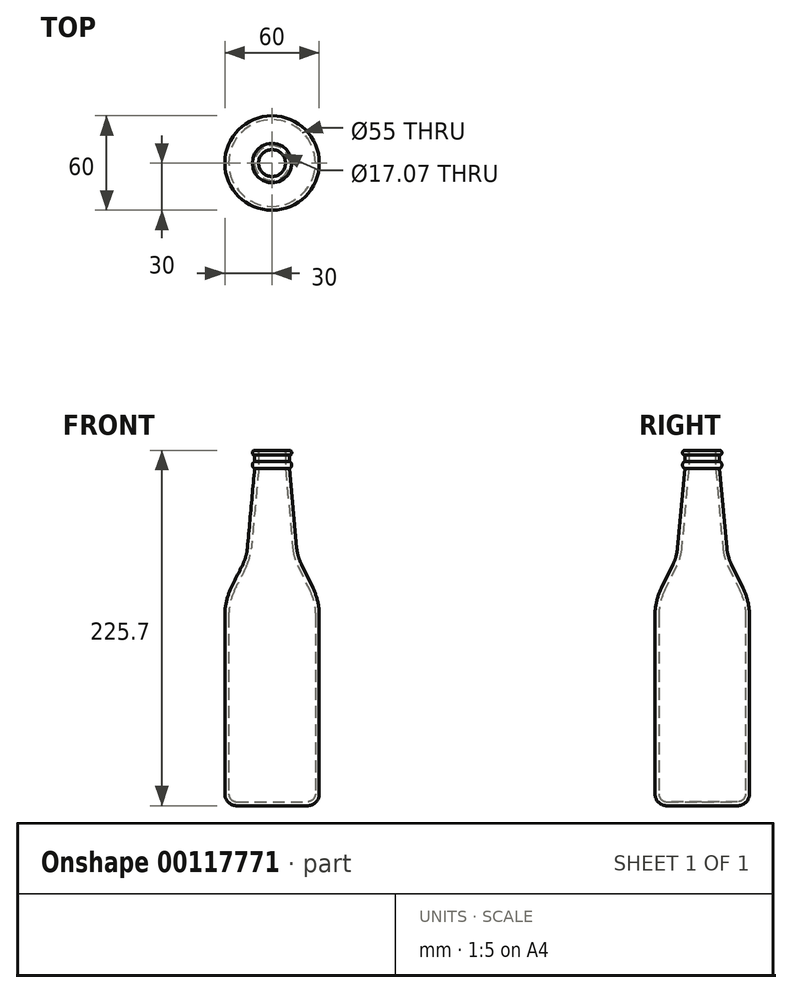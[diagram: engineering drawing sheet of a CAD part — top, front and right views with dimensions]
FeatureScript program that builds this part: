
annotation { "Feature Type Name" : "Feature", "Feature Type Description" : "" }
export const myFeature = defineFeature(function(context is Context, id is Id, definition is map)
    precondition{}
    {
        {
            var Q0;
            Q0=qCreatedBy(makeId("Front.planeOp"),FACE);
            var sketch = newSketch(context, id + "F0", { "sketchPlane" : qUnion([Q0])});
            skLineSegment(sketch, "E0.bottom", {"start": v(0, 0) * mm, "end": v(30, 0) * mm});
            skLineSegment(sketch, "E0.top", {"start": v(0, 130) * mm, "end": v(30, 130) * mm});
            skLineSegment(sketch, "E0.left", {"start": v(0, 0) * mm, "end": v(0, 130) * mm});
            skLineSegment(sketch, "E0.right", {"start": v(30, 0) * mm, "end": v(30, 130) * mm});
            skPoint(sketch, "E1.2.internal.snap0", {"position": v(15, 130) * mm});
            skLineSegment(sketch, "E2", {"start": v(30, 130) * mm, "end": v(16.15, 158.28) * mm});
            skLineSegment(sketch, "E3", {"start": v(16.15, 158.28) * mm, "end": v(11.04, 214.15) * mm});
            skArc(sketch, "E4", {"start": v(11.04, 214.15) * mm, "mid": v(12.5, 216.42) * mm, "end": v(11.04, 218.7) * mm});
            skLineSegment(sketch, "E5", {"start": v(11.04, 218.7) * mm, "end": v(11.04, 222.7) * mm});
            skArc(sketch, "E6", {"start": v(11.04, 222.7) * mm, "mid": v(12.54, 224.2) * mm, "end": v(11.04, 225.7) * mm});
            skLineSegment(sketch, "E7", {"start": v(0, 130) * mm, "end": v(0, 225.7) * mm});
            skLineSegment(sketch, "E8", {"start": v(0, 225.7) * mm, "end": v(11.04, 225.7) * mm});
            skSolve(sketch);
        }
        {
            var Q0;
            Q0 = qSketchRegion(id + "F0", true);
            var Q1;
            Q1=sQuery(id+"F0.wireOp",EDGE,"E0.left");
            revolve(context, id + "F1", {"entities" : qUnion([Q0]), "axis" : qUnion([Q1]), "revolveType" : RevolveType.FULL});
        }
        {
            var Q0;
            Q0=makeQuery(id+"F1.opRevolve","SWEPT_EDGE",EDGE,{"disambiguationData":[OSD([sQuery(id+"F0.wireOp",EDGE,"E0.bottom"),sQuery(id+"F0.wireOp",EDGE,"E0.right")])]});
            fillet(context, id + "F2", {"entities" : qUnion([Q0]), "radius" : 7.5 * mm, "tangentPropagation" : true, "allowEdgeOverflow" : false});
        }
        {
            var Q0;
            Q0=makeQuery(id+"F1.opRevolve","SWEPT_EDGE",EDGE,{"disambiguationData":[OSD([sQuery(id+"F0.wireOp",EDGE,"E0.top"),sQuery(id+"F0.wireOp",EDGE,"E0.right"),sQuery(id+"F0.wireOp",EDGE,"E2")])]});
            fillet(context, id + "F3", {"entities" : qUnion([Q0]), "radius" : 40 * mm, "tangentPropagation" : true, "allowEdgeOverflow" : false});
        }
        {
            var Q0;
            Q0=makeQuery(id+"F1.opRevolve","SWEPT_EDGE",EDGE,{"disambiguationData":[OSD([sQuery(id+"F0.wireOp",EDGE,"E2"),sQuery(id+"F0.wireOp",EDGE,"E3")])]});
            fillet(context, id + "F4", {"entities" : qUnion([Q0]), "radius" : 30 * mm, "tangentPropagation" : true, "allowEdgeOverflow" : false});
        }
        {
            var Q0;
            Q0=makeQuery(id+"F1.opRevolve","SWEPT_FACE",FACE,{"disambiguationData":[OSD([sQuery(id+"F0.wireOp",EDGE,"E8")])]});
            var Q1;
            Q1=makeQuery(id+"F1.opRevolve","SWEPT_BODY",BODY,{"disambiguationData":[OSD([sQuery(id+"F0.wireOp",EDGE,"E0.bottom"),sQuery(id+"F0.wireOp",EDGE,"E0.left"),sQuery(id+"F0.wireOp",EDGE,"E0.right"),sQuery(id+"F0.wireOp",EDGE,"E2"),sQuery(id+"F0.wireOp",EDGE,"E3"),sQuery(id+"F0.wireOp",EDGE,"E4"),sQuery(id+"F0.wireOp",EDGE,"E5"),sQuery(id+"F0.wireOp",EDGE,"E6"),sQuery(id+"F0.wireOp",EDGE,"E7"),sQuery(id+"F0.wireOp",EDGE,"E8")])]});
            shell(context, id + "F5", {"entities" : qUnion([Q0]), "parts" : qUnion([Q1]), "thickness" : 2.5 * mm});
        }
        {
            var Q0;
            Q0=makeQuery(id+"F5.opShell","OFFSET_EDGE",EDGE,{"disambiguationData":[OSD([sQuery(id+"F0.wireOp",EDGE,"E5"),sQuery(id+"F0.wireOp",EDGE,"E6"),sQuery(id+"F0.wireOp",EDGE,"E8")])]});
            fillet(context, id + "F6", {"entities" : qUnion([Q0]), "radius" : 1.5 * mm, "tangentPropagation" : true, "allowEdgeOverflow" : false});
        }
    });
